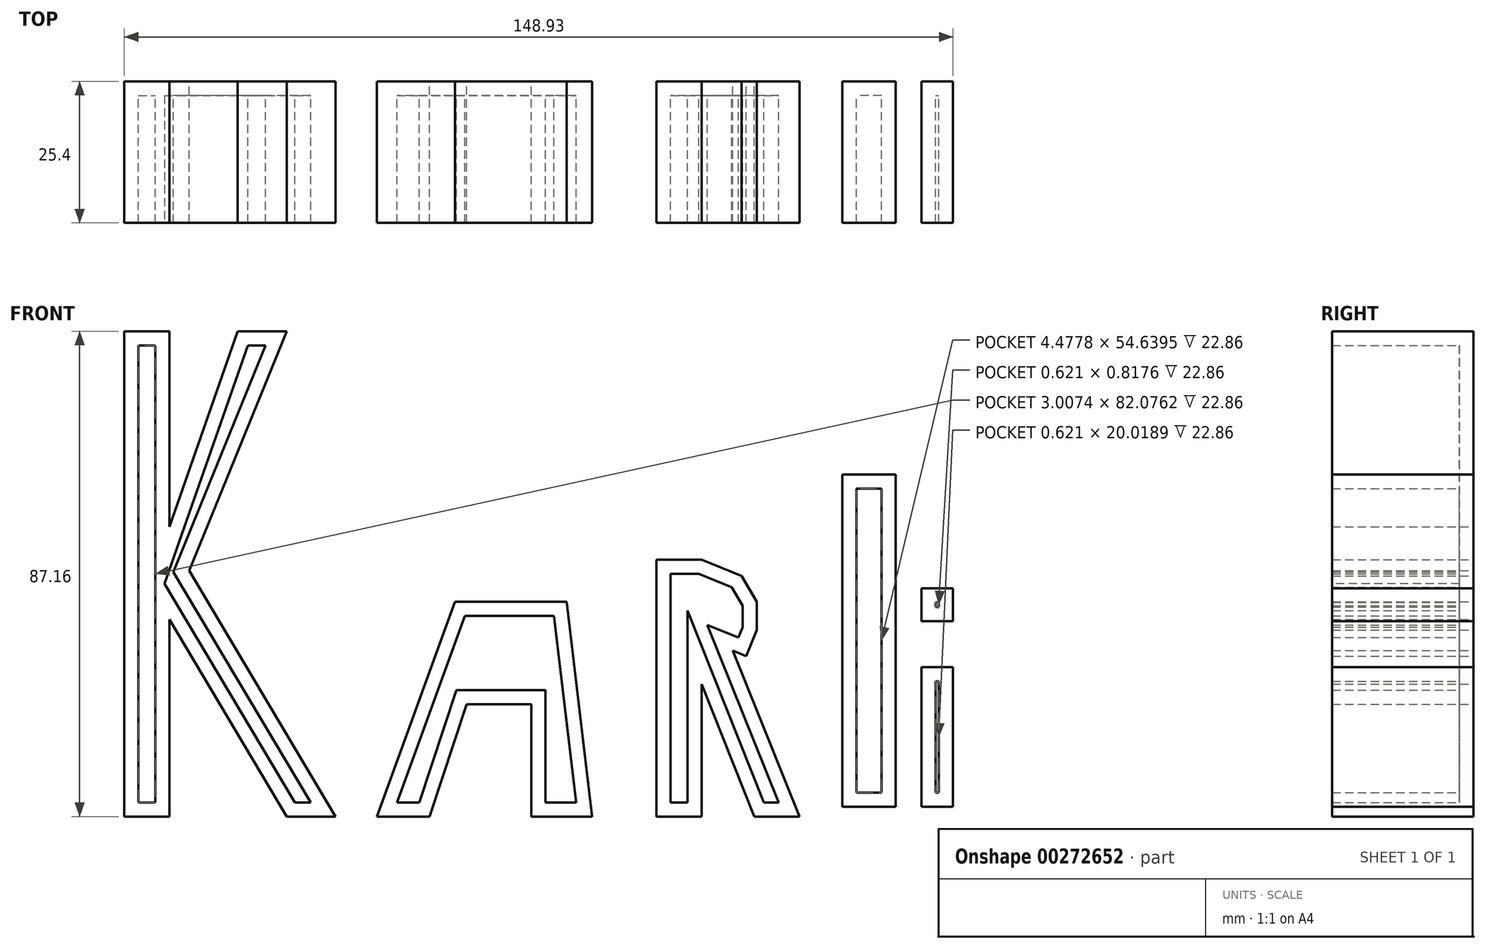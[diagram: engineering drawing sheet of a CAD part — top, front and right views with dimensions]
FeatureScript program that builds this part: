
annotation { "Feature Type Name" : "Feature", "Feature Type Description" : "" }
export const myFeature = defineFeature(function(context is Context, id is Id, definition is map)
    precondition{}
    {
        {
            var Q0;
            Q0=qCreatedBy(makeId("Front.planeOp"),FACE);
            var sketch = newSketch(context, id + "F0", { "sketchPlane" : qUnion([Q0])});
            skLineSegment(sketch, "E0", {"start": v(-69.8, -20.15) * mm, "end": v(-69.8, 67) * mm});
            skLineSegment(sketch, "E1", {"start": v(-69.8, 67) * mm, "end": v(-61.71, 67) * mm});
            skLineSegment(sketch, "E2", {"start": v(-61.71, 67) * mm, "end": v(-61.71, -20.15) * mm});
            skLineSegment(sketch, "E3", {"start": v(-61.71, -20.15) * mm, "end": v(-69.8, -20.15) * mm});
            skLineSegment(sketch, "E4", {"start": v(-61.71, 31.87) * mm, "end": v(-49.4, 67) * mm});
            skLineSegment(sketch, "E5", {"start": v(-49.4, 67) * mm, "end": v(-40.61, 67) * mm});
            skLineSegment(sketch, "E6", {"start": v(-40.61, 67) * mm, "end": v(-61.71, 15.24) * mm});
            skLineSegment(sketch, "E7", {"start": v(-61.71, 15.24) * mm, "end": v(-40.61, -20.15) * mm});
            skLineSegment(sketch, "E8", {"start": v(-40.61, -20.15) * mm, "end": v(-31.82, -20.15) * mm});
            skLineSegment(sketch, "E9", {"start": v(-31.82, -20.15) * mm, "end": v(-58.14, 24) * mm});
            skLineSegment(sketch, "E10", {"start": v(-10.37, 18.45) * mm, "end": v(-24.44, -20.15) * mm});
            skLineSegment(sketch, "E11", {"start": v(-24.44, -20.15) * mm, "end": v(-14.94, -20.15) * mm});
            skLineSegment(sketch, "E12", {"start": v(-14.94, -20.15) * mm, "end": v(-8.26, 0) * mm});
            skLineSegment(sketch, "E13", {"start": v(-8.26, 0) * mm, "end": v(3.34, 0) * mm});
            skLineSegment(sketch, "E14", {"start": v(3.34, 0) * mm, "end": v(3.34, -20.15) * mm});
            skLineSegment(sketch, "E15", {"start": v(3.34, -20.15) * mm, "end": v(14.24, -20.15) * mm});
            skLineSegment(sketch, "E16", {"start": v(14.24, -20.15) * mm, "end": v(9.67, 18.45) * mm});
            skLineSegment(sketch, "E17", {"start": v(9.67, 18.45) * mm, "end": v(-10.37, 18.45) * mm});
            skLineSegment(sketch, "E18", {"start": v(25.84, 18.45) * mm, "end": v(25.84, -20.15) * mm});
            skLineSegment(sketch, "E19", {"start": v(25.84, -20.15) * mm, "end": v(33.93, -20.15) * mm});
            skLineSegment(sketch, "E20", {"start": v(33.93, -20.15) * mm, "end": v(33.93, 3.61) * mm});
            skLineSegment(sketch, "E21", {"start": v(33.93, 3.61) * mm, "end": v(43.43, -20.15) * mm});
            skLineSegment(sketch, "E22", {"start": v(43.43, -20.15) * mm, "end": v(51.51, -20.15) * mm});
            skLineSegment(sketch, "E23", {"start": v(51.51, -20.15) * mm, "end": v(39.56, 9.66) * mm});
            skLineSegment(sketch, "E24", {"start": v(39.56, 9.66) * mm, "end": v(41.95, 8.69) * mm});
            skLineSegment(sketch, "E25", {"start": v(41.95, 8.69) * mm, "end": v(43.85, 13.34) * mm});
            skLineSegment(sketch, "E26", {"start": v(43.85, 13.34) * mm, "end": v(43.85, 18.45) * mm});
            skLineSegment(sketch, "E27", {"start": v(43.85, 18.45) * mm, "end": v(41.1, 23.05) * mm});
            skLineSegment(sketch, "E28", {"start": v(41.1, 23.05) * mm, "end": v(33.93, 25.98) * mm});
            skLineSegment(sketch, "E29", {"start": v(33.93, 25.98) * mm, "end": v(25.84, 25.98) * mm});
            skLineSegment(sketch, "E30", {"start": v(25.84, 25.98) * mm, "end": v(25.84, 6.76) * mm});
            skLineSegment(sketch, "E31", {"start": v(59.23, -18.42) * mm, "end": v(59.23, 41.3) * mm});
            skLineSegment(sketch, "E32", {"start": v(59.23, 41.3) * mm, "end": v(68.8, 41.3) * mm});
            skLineSegment(sketch, "E33", {"start": v(68.8, 41.3) * mm, "end": v(68.8, -18.42) * mm});
            skLineSegment(sketch, "E34", {"start": v(68.8, -18.42) * mm, "end": v(59.23, -18.42) * mm});
            skLineSegment(sketch, "E35", {"start": v(73.42, 6.68) * mm, "end": v(73.42, -18.42) * mm});
            skLineSegment(sketch, "E36", {"start": v(73.42, -18.42) * mm, "end": v(79.13, -18.42) * mm});
            skLineSegment(sketch, "E37", {"start": v(79.13, -18.42) * mm, "end": v(79.13, 6.68) * mm});
            skLineSegment(sketch, "E38", {"start": v(79.13, 6.68) * mm, "end": v(73.42, 6.68) * mm});
            skLineSegment(sketch, "E39", {"start": v(73.42, 20.84) * mm, "end": v(73.42, 14.94) * mm});
            skLineSegment(sketch, "E40", {"start": v(73.42, 14.94) * mm, "end": v(79.13, 14.94) * mm});
            skLineSegment(sketch, "E41", {"start": v(73.42, 20.84) * mm, "end": v(79.13, 20.84) * mm});
            skLineSegment(sketch, "E42", {"start": v(79.13, 20.84) * mm, "end": v(79.13, 14.94) * mm});
            skSolve(sketch);
        }
        {
            var Q0;
            Q0 = qSketchRegion(id + "F0", true);
            extrude(context, id + "F1", {"entities" : qUnion([Q0]), "depth" : 25.4 * mm});
        }
        {
            var Q0;
            Q0=makeQuery(id+"F1.opExtrude","CAP_FACE",FACE,{"disambiguationData":[OSD([sQuery(id+"F0.wireOp",EDGE,"E10"),sQuery(id+"F0.wireOp",EDGE,"E11"),sQuery(id+"F0.wireOp",EDGE,"E12"),sQuery(id+"F0.wireOp",EDGE,"E13"),sQuery(id+"F0.wireOp",EDGE,"E14"),sQuery(id+"F0.wireOp",EDGE,"E15"),sQuery(id+"F0.wireOp",EDGE,"E16"),sQuery(id+"F0.wireOp",EDGE,"E17")])],"isStart":false});
            shell(context, id + "F2", {"entities" : qUnion([Q0]), "thickness" : 2.54 * mm});
        }
        {
            var Q0;
            Q0=makeQuery(id+"F1.opExtrude","CAP_FACE",FACE,{"disambiguationData":[OSD([sQuery(id+"F0.wireOp",EDGE,"E31"),sQuery(id+"F0.wireOp",EDGE,"E32"),sQuery(id+"F0.wireOp",EDGE,"E33"),sQuery(id+"F0.wireOp",EDGE,"E34")])],"isStart":false});
            shell(context, id + "F3", {"entities" : qUnion([Q0]), "thickness" : 2.54 * mm});
        }
        {
            var Q0;
            Q0=makeQuery(id+"F1.opExtrude","CAP_FACE",FACE,{"disambiguationData":[OSD([sQuery(id+"F0.wireOp",EDGE,"E18"),sQuery(id+"F0.wireOp",EDGE,"E19"),sQuery(id+"F0.wireOp",EDGE,"E20"),sQuery(id+"F0.wireOp",EDGE,"E21"),sQuery(id+"F0.wireOp",EDGE,"E22"),sQuery(id+"F0.wireOp",EDGE,"E23"),sQuery(id+"F0.wireOp",EDGE,"E24"),sQuery(id+"F0.wireOp",EDGE,"E25"),sQuery(id+"F0.wireOp",EDGE,"E26"),sQuery(id+"F0.wireOp",EDGE,"E27"),sQuery(id+"F0.wireOp",EDGE,"E28"),sQuery(id+"F0.wireOp",EDGE,"E29"),sQuery(id+"F0.wireOp",EDGE,"E30")])],"isStart":false});
            shell(context, id + "F4", {"entities" : qUnion([Q0]), "thickness" : 2.54 * mm});
        }
        {
            var Q0;
            Q0=makeQuery(id+"F1.opExtrude","CAP_FACE",FACE,{"disambiguationData":[OSD([sQuery(id+"F0.wireOp",EDGE,"E0"),sQuery(id+"F0.wireOp",EDGE,"E1"),sQuery(id+"F0.wireOp",EDGE,"E2"),sQuery(id+"F0.wireOp",EDGE,"E3"),sQuery(id+"F0.wireOp",EDGE,"E4"),sQuery(id+"F0.wireOp",EDGE,"E5"),sQuery(id+"F0.wireOp",EDGE,"E6"),sQuery(id+"F0.wireOp",EDGE,"E7"),sQuery(id+"F0.wireOp",EDGE,"E8"),sQuery(id+"F0.wireOp",EDGE,"E9")])],"isStart":false});
            shell(context, id + "F5", {"entities" : qUnion([Q0]), "thickness" : 2.54 * mm});
        }
        {
            var Q0;
            Q0=makeQuery(id+"F1.opExtrude","CAP_FACE",FACE,{"disambiguationData":[OSD([sQuery(id+"F0.wireOp",EDGE,"E35"),sQuery(id+"F0.wireOp",EDGE,"E36"),sQuery(id+"F0.wireOp",EDGE,"E37"),sQuery(id+"F0.wireOp",EDGE,"E38")])],"isStart":false});
            var Q1;
            Q1=makeQuery(id+"F1.opExtrude","CAP_FACE",FACE,{"disambiguationData":[OSD([sQuery(id+"F0.wireOp",EDGE,"E39"),sQuery(id+"F0.wireOp",EDGE,"E40"),sQuery(id+"F0.wireOp",EDGE,"E41"),sQuery(id+"F0.wireOp",EDGE,"E42")])],"isStart":false});
            shell(context, id + "F6", {"entities" : qUnion([Q0, Q1]), "thickness" : 2.54 * mm});
        }
    });
